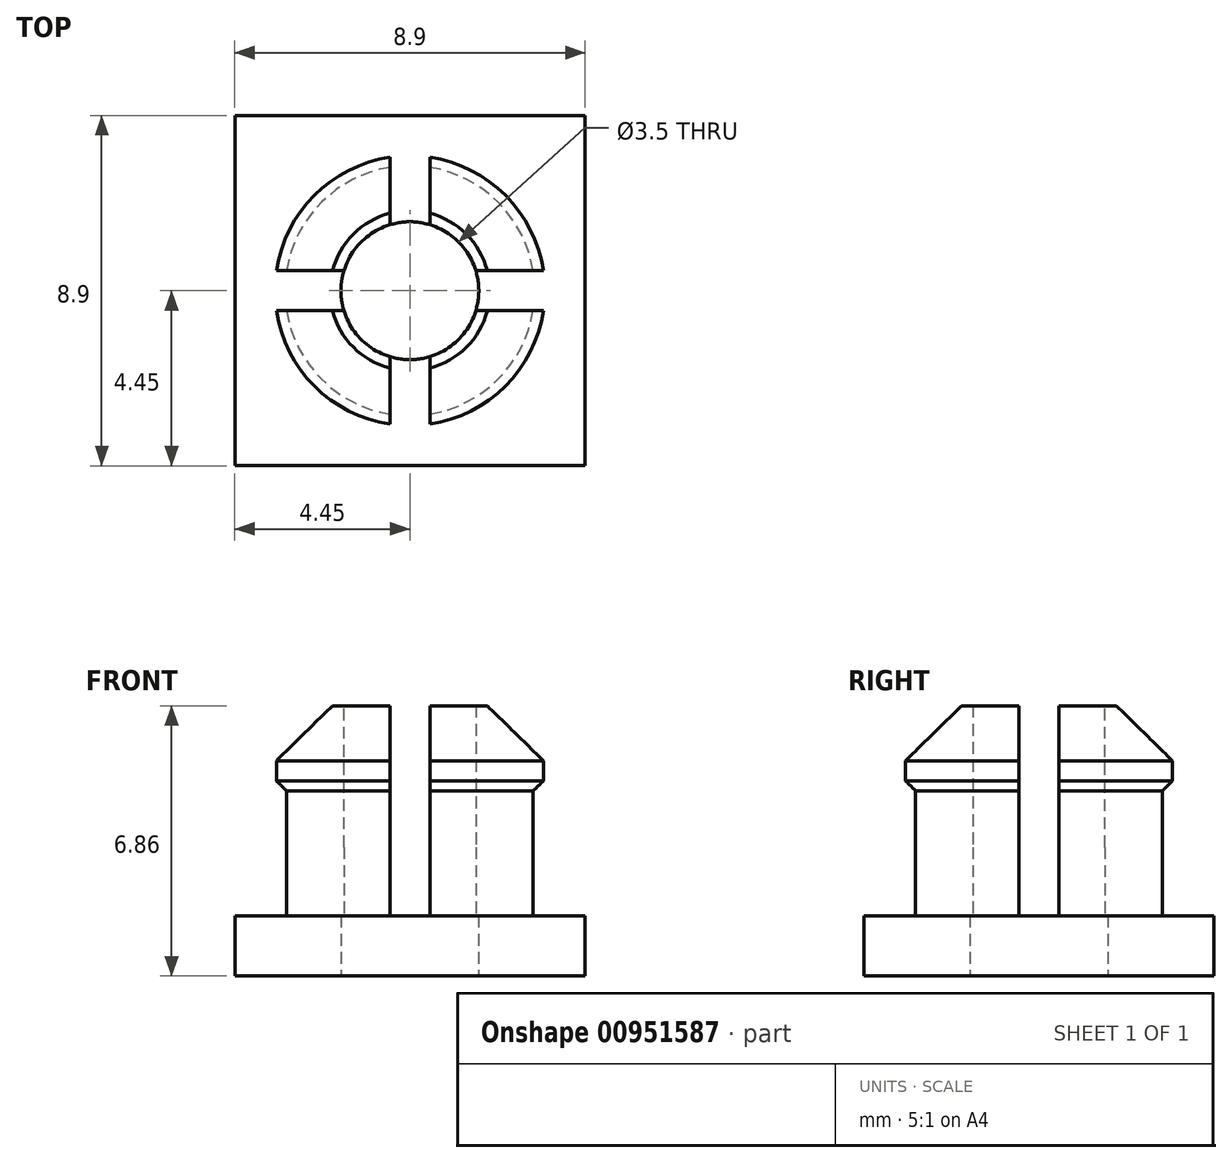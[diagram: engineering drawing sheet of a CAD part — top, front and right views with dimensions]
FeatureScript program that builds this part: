
annotation { "Feature Type Name" : "Feature", "Feature Type Description" : "" }
export const myFeature = defineFeature(function(context is Context, id is Id, definition is map)
    precondition{}
    {
        {
            var Q0;
            Q0=qCreatedBy(makeId("Front.planeOp"),FACE);
            var sketch = newSketch(context, id + "F0", { "sketchPlane" : qUnion([Q0])});
            skLineSegment(sketch, "E0", {"start": v(0, 0) * mm, "end": v(0, 3.04) * mm});
            skLineSegment(sketch, "E1", {"start": v(-1.75, 8.38) * mm, "end": v(-2.03, 8.38) * mm});
            skLineSegment(sketch, "E2", {"start": v(-2.03, 8.38) * mm, "end": v(-3.43, 6.98) * mm});
            skLineSegment(sketch, "E3", {"start": v(-3.43, 6.48) * mm, "end": v(-3.18, 6.22) * mm});
            skLineSegment(sketch, "E4", {"start": v(-3.18, 6.22) * mm, "end": v(-3.18, 3.05) * mm});
            skLineSegment(sketch, "E5", {"start": v(-3.18, 3.05) * mm, "end": v(-6.73, 3.05) * mm});
            skPoint(sketch, "E6.end.orphan", {"position": v(0, -0.24) * mm});
            skLineSegment(sketch, "E7", {"start": v(-8.13, 0) * mm, "end": v(0, 0) * mm});
            skLineSegment(sketch, "E8", {"start": v(-6.73, 3.05) * mm, "end": v(-6.73, 2.03) * mm});
            skLineSegment(sketch, "E9", {"start": v(-6.73, 2.03) * mm, "end": v(-9.14, 2.03) * mm});
            skLineSegment(sketch, "E10", {"start": v(-9.14, 1.02) * mm, "end": v(-8.13, 0) * mm});
            skLineSegment(sketch, "E11", {"start": v(-3.43, 6.48) * mm, "end": v(-3.43, 6.98) * mm});
            skPoint(sketch, "E12.orphan", {"position": v(-3.68, 6.73) * mm});
            skLineSegment(sketch, "E13", {"start": v(-1.75, 8.38) * mm, "end": v(-1.75, 4.8) * mm});
            skLineSegment(sketch, "E14", {"start": v(0, 3.04) * mm, "end": v(-1.75, 4.8) * mm});
            skLineSegment(sketch, "E15", {"start": v(-9.14, 2.03) * mm, "end": v(-9.14, -0.7) * mm});
            skPoint(sketch, "E16.orphan", {"position": v(-10.16, 2.03) * mm});
            skSolve(sketch);
        }
        {
            var Q0;
            Q0=makeQuery(id+"F0.imprint","IMPRINT",FACE,{"disambiguationData":[TD([[makeQuery(id+"F0.imprint","IMPRINT",EDGE,{"derivedFrom":sQuery(id+"F0.wireOp",EDGE,"E0")}),1.0]])]});
            var Q1;
            Q1=sQuery(id+"F0.wireOp",EDGE,"E0");
            revolve(context, id + "F1", {"surfaceOperationType" : NewSurfaceOperationType.NEW, "entities" : qUnion([Q0]), "axis" : qUnion([Q1]), "revolveType" : RevolveType.FULL});
        }
        {
            var Q0;
            Q0=makeQuery(id+"F1.opRevolve","SWEPT_FACE",FACE,{"disambiguationData":[OSD([sQuery(id+"F0.wireOp",EDGE,"E1")])]});
            var sketch = newSketch(context, id + "F2", { "sketchPlane" : qUnion([Q0])});
            skLineSegment(sketch, "E17.bottom", {"start": v(0.5, -3.94) * mm, "end": v(-0.5, -3.94) * mm});
            skLineSegment(sketch, "E17.top", {"start": v(0.5, 3.94) * mm, "end": v(-0.5, 3.94) * mm});
            skLineSegment(sketch, "E17.left", {"start": v(0.5, -3.94) * mm, "end": v(0.5, 3.94) * mm});
            skLineSegment(sketch, "E17.right", {"start": v(-0.5, -3.94) * mm, "end": v(-0.5, 3.94) * mm});
            skPoint(sketch, "E17.middle", {"position": v(0, 0) * mm});
            skLineSegment(sketch, "E18.bottom", {"start": v(3.9, 0.5) * mm, "end": v(-3.9, 0.5) * mm});
            skLineSegment(sketch, "E18.top", {"start": v(3.9, -0.5) * mm, "end": v(-3.9, -0.5) * mm});
            skLineSegment(sketch, "E18.left", {"start": v(3.9, 0.5) * mm, "end": v(3.9, -0.5) * mm});
            skLineSegment(sketch, "E18.right", {"start": v(-3.9, 0.5) * mm, "end": v(-3.9, -0.5) * mm});
            skSolve(sketch);
        }
        {
            var Q0;
            {var subQ0=sQuery(id+"F2.wireOp",EDGE,"E18.bottom");var subQ1=sQuery(id+"F0.wireOp",EDGE,"E1");var subQ2=makeQuery(id+"F1.opRevolve","SWEPT_EDGE",EDGE,{"disambiguationData":[OSD([subQ1,sQuery(id+"F0.wireOp",EDGE,"E2")])]});var subQ3=makeQuery(id+"F2.imprint","INTERSECT",VERTEX,{"disambiguationData":[OD(0.0)],"derivedFrom":[subQ2,subQ0]});Q0=makeQuery(id+"F2.imprint","IMPRINT",FACE,{"disambiguationData":[TD([[makeQuery(id+"F2.imprint","IMPRINT",EDGE,{"disambiguationData":[TD([[subQ3,-1.0]])],"derivedFrom":subQ0}),1.0]])]});}
            var Q1;
            {var subQ0=sQuery(id+"F2.wireOp",EDGE,"E17.left");var subQ1=sQuery(id+"F0.wireOp",EDGE,"E1");var subQ2=makeQuery(id+"F1.opRevolve","SWEPT_EDGE",EDGE,{"disambiguationData":[OSD([subQ1,sQuery(id+"F0.wireOp",EDGE,"E2")])]});var subQ3=makeQuery(id+"F2.imprint","INTERSECT",VERTEX,{"disambiguationData":[OD(0.0)],"derivedFrom":[subQ2,subQ0]});Q1=makeQuery(id+"F2.imprint","IMPRINT",FACE,{"disambiguationData":[TD([[makeQuery(id+"F2.imprint","IMPRINT",EDGE,{"disambiguationData":[TD([[subQ3,-1.0]])],"derivedFrom":subQ0}),1.0]])]});}
            var Q2;
            {var subQ0=sQuery(id+"F2.wireOp",EDGE,"E17.left");var subQ1=sQuery(id+"F0.wireOp",EDGE,"E1");var subQ2=makeQuery(id+"F1.opRevolve","SWEPT_EDGE",EDGE,{"disambiguationData":[OSD([subQ1,sQuery(id+"F0.wireOp",EDGE,"E2")])]});var subQ3=makeQuery(id+"F2.imprint","INTERSECT",VERTEX,{"disambiguationData":[OD(1.0)],"derivedFrom":[subQ2,subQ0]});Q2=makeQuery(id+"F2.imprint","IMPRINT",FACE,{"disambiguationData":[TD([[makeQuery(id+"F2.imprint","IMPRINT",EDGE,{"disambiguationData":[TD([[subQ3,1.0]])],"derivedFrom":subQ0}),1.0]])]});}
            var Q3;
            {var subQ0=sQuery(id+"F2.wireOp",EDGE,"E18.bottom");var subQ1=sQuery(id+"F0.wireOp",EDGE,"E1");var subQ2=makeQuery(id+"F1.opRevolve","SWEPT_EDGE",EDGE,{"disambiguationData":[OSD([subQ1,sQuery(id+"F0.wireOp",EDGE,"E2")])]});var subQ3=makeQuery(id+"F2.imprint","INTERSECT",VERTEX,{"disambiguationData":[OD(1.0)],"derivedFrom":[subQ2,subQ0]});Q3=makeQuery(id+"F2.imprint","IMPRINT",FACE,{"disambiguationData":[TD([[makeQuery(id+"F2.imprint","IMPRINT",EDGE,{"disambiguationData":[TD([[subQ3,1.0]])],"derivedFrom":subQ0}),1.0]])]});}
            var Q4;
            {var subQ0=sQuery(id+"F2.wireOp",EDGE,"E17.bottom");Q4=makeQuery(id+"F2.imprint","IMPRINT",FACE,{"disambiguationData":[TD([[makeQuery(id+"F2.imprint","IMPRINT",EDGE,{"derivedFrom":subQ0}),-1.0]])]});}
            var Q5;
            {var subQ0=sQuery(id+"F2.wireOp",EDGE,"E18.left");Q5=makeQuery(id+"F2.imprint","IMPRINT",FACE,{"disambiguationData":[TD([[makeQuery(id+"F2.imprint","IMPRINT",EDGE,{"derivedFrom":subQ0}),-1.0]])]});}
            var Q6;
            {var subQ0=sQuery(id+"F2.wireOp",EDGE,"E18.right");Q6=makeQuery(id+"F2.imprint","IMPRINT",FACE,{"disambiguationData":[TD([[makeQuery(id+"F2.imprint","IMPRINT",EDGE,{"derivedFrom":subQ0}),1.0]])]});}
            var Q7;
            {var subQ0=sQuery(id+"F2.wireOp",EDGE,"E17.top");Q7=makeQuery(id+"F2.imprint","IMPRINT",FACE,{"disambiguationData":[TD([[makeQuery(id+"F2.imprint","IMPRINT",EDGE,{"derivedFrom":subQ0}),1.0]])]});}
            extrude(context, id + "F3", {"entities" : qUnion([Q0, Q1, Q2, Q3, Q4, Q5, Q6, Q7]), "operationType" : NewBodyOperationType.REMOVE, "oppositeDirection" : true, "depth" : 5.33 * mm, "offsetDistance" : 25.4 * mm});
        }
        {
            var Q0;
            Q0=makeQuery(id+"F1.opRevolve","SWEPT_FACE",FACE,{"disambiguationData":[OSD([sQuery(id+"F0.wireOp",EDGE,"E7")])]});
            var sketch = newSketch(context, id + "F4", { "sketchPlane" : qUnion([Q0])});
            skCircle(sketch, "E19", {"center": v(0, 0) * mm, "radius": 1.75 * mm});
            skSolve(sketch);
        }
        {
            var Q0;
            Q0 = qSketchRegion(id + "F4", true);
            extrude(context, id + "F5", {"entities" : qUnion([Q0]), "operationType" : NewBodyOperationType.REMOVE, "oppositeDirection" : true, "depth" : 25.4 * mm, "offsetDistance" : 25.4 * mm});
        }
        {
            var Q0;
            Q0=makeQuery(id+"F4.imprint","IMPRINT",FACE,{"disambiguationData":[TD([[makeQuery(id+"F4.imprint","IMPRINT",EDGE,{"derivedFrom":sQuery(id+"F4.wireOp",EDGE,"E19")}),-1.0]])]});
            var sketch = newSketch(context, id + "F6", { "sketchPlane" : qUnion([Q0])});
            skLineSegment(sketch, "E20.bottom", {"start": v(4.44, -4.45) * mm, "end": v(-4.44, -4.45) * mm});
            skLineSegment(sketch, "E20.top", {"start": v(4.45, 4.45) * mm, "end": v(-4.44, 4.44) * mm});
            skLineSegment(sketch, "E20.left", {"start": v(4.45, -4.44) * mm, "end": v(4.45, 4.45) * mm});
            skLineSegment(sketch, "E20.right", {"start": v(-4.44, -4.45) * mm, "end": v(-4.44, 4.44) * mm});
            skPoint(sketch, "E20.middle", {"position": v(0, 0) * mm});
            skSolve(sketch);
        }
        {
            var Q0;
            Q0 = qSketchRegion(id + "F6", true);
            extrude(context, id + "F7", {"entities" : qUnion([Q0]), "operationType" : NewBodyOperationType.INTERSECT, "oppositeDirection" : true, "depth" : 25.4 * mm, "offsetDistance" : 25.4 * mm});
        }
        {
            var Q0;
            Q0 = qSketchRegion(id + "F6", true);
            extrude(context, id + "F8", {"entities" : qUnion([Q0]), "operationType" : NewBodyOperationType.REMOVE, "oppositeDirection" : true, "depth" : 1.52 * mm, "offsetDistance" : 25.4 * mm});
        }
    });
